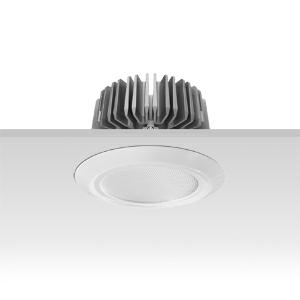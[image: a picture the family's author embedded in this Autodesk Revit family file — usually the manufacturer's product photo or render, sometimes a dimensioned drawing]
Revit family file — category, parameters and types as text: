
# Revit family: 3f_filippi_-_3f_reno_bianco_ampio_3f_filippi_-_30375_a01035_-_3f_reno_150_wh_2000-840_dali_wide___vs_wh_6218
name_source: partatom
category: Lighting Fixtures
units: mm (PartAtom-declared; Revit-internal decimal feet)

## family parameters
Cut with Voids When Loaded = No
Host = Face
Light Source = No
Part Type = Normal
Room Calculation Point = No
Round Connector Dimension = Use Diameter
Shared = No

## types (1)
- 3F Filippi - 3F Reno Bianco Ampio (1 x LED, 1709 lm, 20 W, 4000 K)
    Apparent Load = 20 VA
    Approval mark = CE
    CIE Flux Codes = 74 93 99 100 100
    Color Rendering = 80
    Color Temperature = 4000 K
    Control Gear = Electronic transformer
    Default Elevation = 1800 mm
    Description = ILLUMINOTECHNICAL
Luminous efficiency 100% (DLOR 100%, ULOR 0%).
Initial luminous flux of the luminaire 1709 lm.
Direct symmetric wide distribution.
Installation Interdistance Transv.D = 1.12 x hu - Long.D = 1.11 x hu.
Tabular UGR (CIE 117 - 4H-8H; S=0.25H; 70/50/20): RUG 22.8 - 22.7.
Beam angle: 74° - 73°.
Luminous efficacy 85 lm/W.
Lifetime (L90/B10): 30000 h. (tq+25°C)
Lifetime (L85/B10): 50000 h. (tq+25°C)
Lifetime (L70/B10): 80000 h. (tq+25°C)
Sudden decreased luminous flux after 50000 hours: 0% (C0).
Photobiological safety in compliance with IEC/TR 62778: RG0 risk exempt, (IEC 62471).
In compliance with IEC/EN 62722-2-1 - IEC/EN 62717 standards.

SOURCE
Compact LED module 2000/840.
Energy efficiency class (UE 2019/2020 - UE 2019/2015): D.
CIE 13.3 Colour rendering index: CRI >80 (R9 <50%).
IES TM-30 Fidelity Index: Rf = 84 Rg = 95.
CCT nominal colour temperature 4000 K.
Colour initial tolerance (MacAdam): SDCM 3.
Zhaga Book 3 compliant.

MECHANICAL
Passive heat dissipator in die-casting aluminium, oversized, for optimum thermal management of the LED module.
Parabolic element with graduated/concentric rings in white polycarbonate.
Transparent external lens with glossy and satin differentiated surfaces, with a cooling and anti-insect system in methacrylate (PMMA).
Fastening spring clips in stainless steel.
Dimensions: diameter 176 mm, height 111 mm. Weight 0.88 kg.
IP44 protection degree for exposed part, IP20 for recessed part.
Mechanical strength to impacts IK06 (1 joule).
Glow-wire test resistance 650°C.

ELECTRICAL
Wiring on a separate unit.
Halogen Free DALI-2 DATI (Parts 251, 252, 253), PUSH-DIM, electronic wiring 230V-50/60Hz, power factor 0.90 at full load, THD <25%, constant output current, SELV, class II, 1 driver, 1 DALI addresse.
Power of the luminaire 20 W.
ENEC - CE.
SAFE FLICKER: PstLM=<1 and SVM=<0.4 (IEC TR 61547-1 and IEC TR 63158), to ensure a more comfortable and safe light.
Luminaire compliant with EN 60598-2-22 for power supply from a centralised emergency system CPSS (Central Power Supply System), not incorporated in the luminaire - high risk areas excluded. The default power and flux are 100% in AC and 100% in DC.
Ambient temperature from 0°C to +25°C.
Temperature class T6 max 85°C.
Relative humidity UR: <85%.

INSTALLATION
Pull-up recessed fitting.
False ceiling carving: 150 mm.
All accessories dedicated to this product are available on the Catalog and on our website www.3F-Filippi.com.

ACCESSORIES
A01035 - Anti-glare microprismatic VS moulded glass, tempered, not flammable, locked and in line with the trim, in white polycarbonate.

APPLICATIONS
Environments: architectural, commercial, exhibition areas, transit areas, corridors, shops, display windows, service areas.
In false ceilings with narrow voids.

LIGHT MANAGEMENT
Recommended minimum setting: 10%.
The luminaire, equipped with (DALI-2 DATI) driver, can be controlled manually with 3F Easy Dim technology or automatically/manually with wired or wireless DALI/D2D control systems.
The D2D driver guarantees interoperability with other devices with the same certification by making the following information available:
Device Data (Part 251), Energy Report (Part 252), Diagnosis & Maintenance (Part 253).
In electrical systems without a regulation system (manual or automatic) and DALI bus, a suitable jumper must be made on the DA-DA terminals of the appliance.

WARNING
Luminaire designed for disposal/recycling at end-of-life.
Replaceable (LED only) light source by a professional. Replaceable control gear by a professional.
    Height = 0 mm  [stored 0 ft]
    Lamp = 1 x LED
    Lamp Light Flux = 1709 lm
    Lamp Power = 20 W
    Lamp count = 1
    Length = 176 mm
    Lifetime = 50000 h
    Luminous efficacy = 85 lm/W
    Manufacturer = 3F Filippi
    ModVariant = No
    Model = 3F Filippi - 30375+A01035 - 3F Reno 150 WH 2000-840 DALI WIDE + VS WH
    Mounting Place = Ceiling
    Mounting Type = Recessed
    Number of Poles = 1
    OnlyDefault = Yes
    Power Factor = 1
    Product Name = 3F Filippi - 3F Reno Bianco Ampio
    Product group = recessed luminaire
    ProductGroupID = 4
    Protection Class = Protection class II
    Protection Degree = IP 20
    RLX_Detail_Level = 1
    RLX_Emergency_Light_Flux = 0 lm
    RLX_Emergency_Type = 0
    RLX_Emergency_Type_DB = No
    RlxData = <blob elided: 84569 chars, md5=fa1c2590>
    Socket = socket
    Standby Power = 0 W
    System Light Flux = 1709 lm
    System Power = 20 W
    Type Comments = Product without accessories
    Type Image = 3ffilippi_3f_reno_150_wh_vs_smp.jpg
    URL = http://relux.com
    VarID = ---
    Voltage = 0 V
    Weight = 0.00 kg
    Width = 0 mm  [stored 0 ft]

note: [stored X ft] marks values corroborated as IEEE doubles in the binary element streams (Revit-internal decimal feet)

## geometry (parser evidence)
native form markers: Blend x4, Sweep x12
no freeform markers — native parametric forms only
